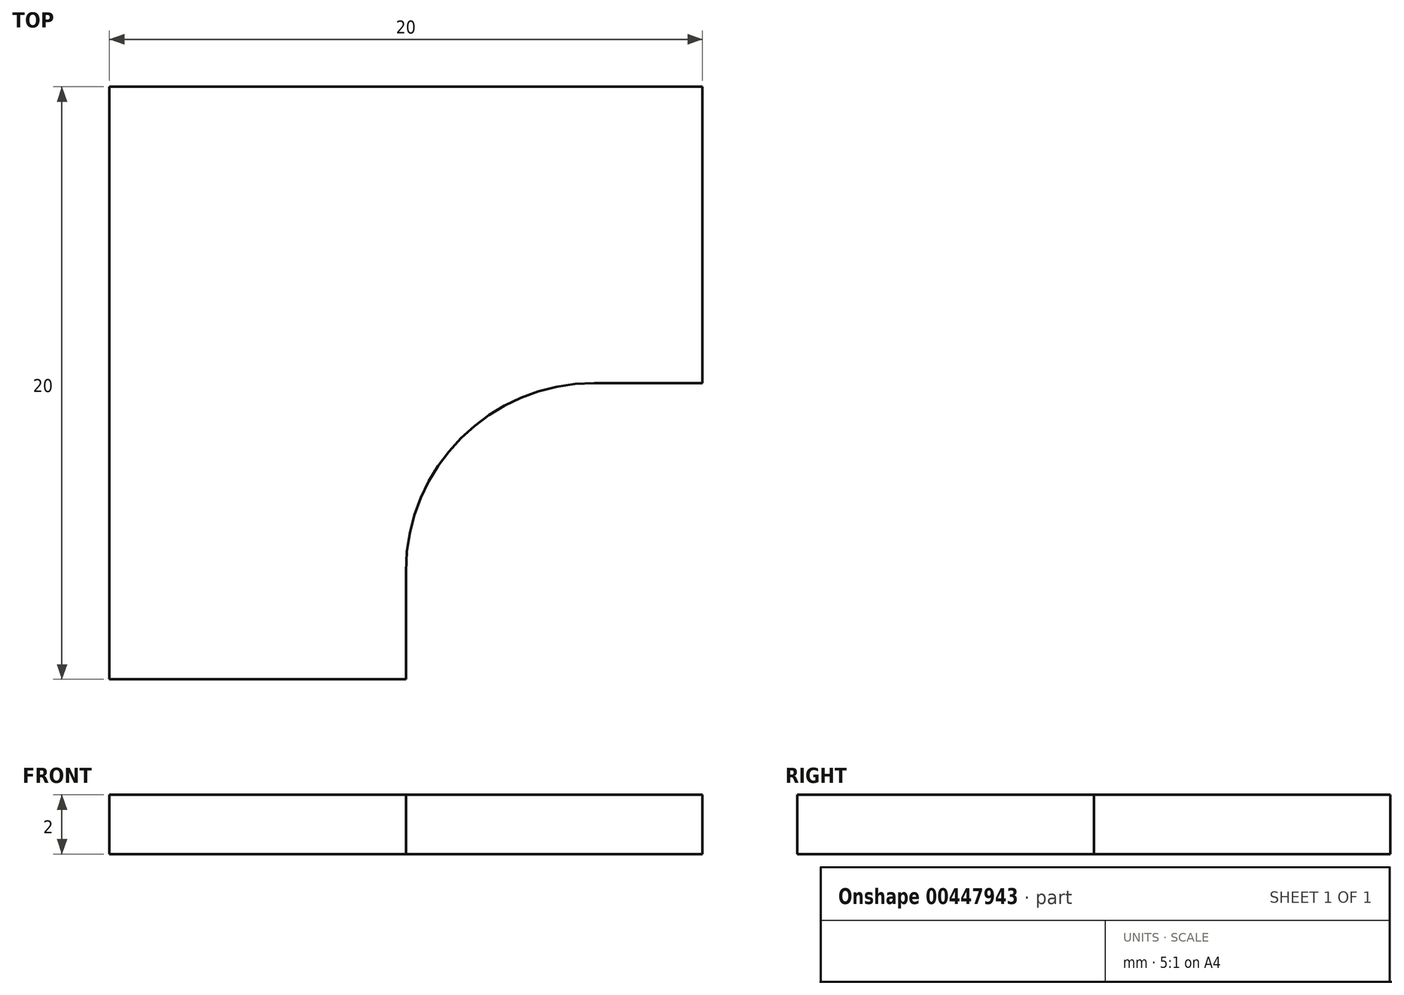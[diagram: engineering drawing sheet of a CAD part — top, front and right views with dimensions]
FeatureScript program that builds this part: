
annotation { "Feature Type Name" : "Feature", "Feature Type Description" : "" }
export const myFeature = defineFeature(function(context is Context, id is Id, definition is map)
    precondition{}
    {
        {
            var Q0;
            Q0=qCreatedBy(makeId("Top.planeOp"),FACE);
            var sketch = newSketch(context, id + "F0", { "sketchPlane" : qUnion([Q0])});
            skLineSegment(sketch, "E0", {"start": v(0, 0) * mm, "end": v(20, 0) * mm});
            skLineSegment(sketch, "E1", {"start": v(20, 0) * mm, "end": v(20, -10) * mm});
            skLineSegment(sketch, "E2", {"start": v(20, -10) * mm, "end": v(16.35, -10) * mm});
            skLineSegment(sketch, "E3", {"start": v(10, -16.35) * mm, "end": v(10, -20) * mm});
            skLineSegment(sketch, "E4", {"start": v(10, -20) * mm, "end": v(0, -20) * mm});
            skLineSegment(sketch, "E5", {"start": v(0, -20) * mm, "end": v(0, 0) * mm});
            skPoint(sketch, "E6.visualSharp", {"position": v(10, -10) * mm});
            skArc(sketch, "E6.filletArc", {"start": v(16.35, -10) * mm, "mid": v(11.86, -11.86) * mm, "end": v(10, -16.35) * mm});
            skSolve(sketch);
        }
        {
            var Q0;
            Q0=makeQuery(id+"F0.imprint","IMPRINT",FACE,{"disambiguationData":[TD([[makeQuery(id+"F0.imprint","IMPRINT",EDGE,{"derivedFrom":sQuery(id+"F0.wireOp",EDGE,"E0")}),-1.0]])]});
            extrude(context, id + "F1", {"entities" : qUnion([Q0]), "depth" : 2 * mm});
        }
    });
